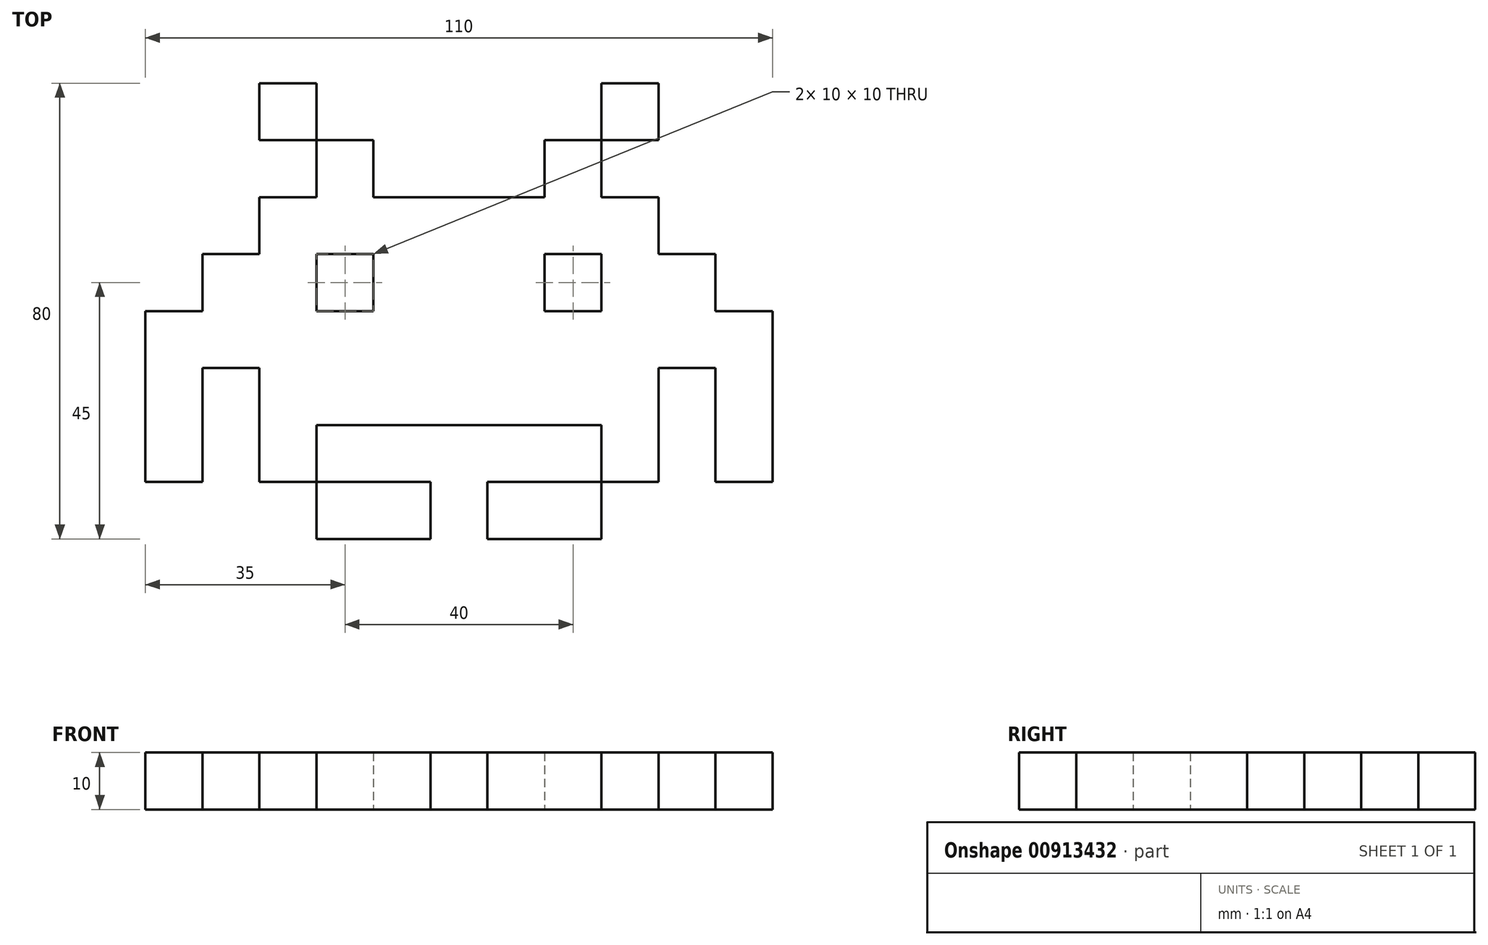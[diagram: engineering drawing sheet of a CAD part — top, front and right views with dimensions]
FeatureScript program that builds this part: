
annotation { "Feature Type Name" : "Feature", "Feature Type Description" : "" }
export const myFeature = defineFeature(function(context is Context, id is Id, definition is map)
    precondition{}
    {
        {
            var Q0;
            Q0=qCreatedBy(makeId("Top.planeOp"),FACE);
            var sketch = newSketch(context, id + "F0", { "sketchPlane" : qUnion([Q0])});
            skLineSegment(sketch, "E0", {"start": v(-15, 5) * mm, "end": v(-15, -5) * mm});
            skLineSegment(sketch, "E1", {"start": v(-15, -5) * mm, "end": v(-25, -5) * mm});
            skLineSegment(sketch, "E2", {"start": v(-25, -5) * mm, "end": v(-25, 5) * mm});
            skLineSegment(sketch, "E3", {"start": v(-25, 5) * mm, "end": v(-15, 5) * mm});
            skLineSegment(sketch, "E4", {"start": v(15, 5) * mm, "end": v(15, -5) * mm});
            skLineSegment(sketch, "E5", {"start": v(15, -5) * mm, "end": v(25, -5) * mm});
            skLineSegment(sketch, "E6", {"start": v(25, -5) * mm, "end": v(25, 5) * mm});
            skLineSegment(sketch, "E7", {"start": v(25, 5) * mm, "end": v(15, 5) * mm});
            skPoint(sketch, "E8", {"position": v(-15, 0) * mm});
            skPoint(sketch, "E9", {"position": v(15, 0) * mm});
            skLineSegment(sketch, "E10", {"start": v(-15, 15) * mm, "end": v(15, 15) * mm});
            skLineSegment(sketch, "E11", {"start": v(15, 15) * mm, "end": v(15, 25) * mm});
            skLineSegment(sketch, "E12", {"start": v(15, 25) * mm, "end": v(25, 25) * mm});
            skLineSegment(sketch, "E13", {"start": v(25, 25) * mm, "end": v(25, 15) * mm});
            skLineSegment(sketch, "E14", {"start": v(25, 15) * mm, "end": v(35, 15) * mm});
            skLineSegment(sketch, "E15", {"start": v(35, 15) * mm, "end": v(35, 5) * mm});
            skLineSegment(sketch, "E16", {"start": v(35, 5) * mm, "end": v(45, 5) * mm});
            skLineSegment(sketch, "E17", {"start": v(45, 5) * mm, "end": v(45, -5) * mm});
            skLineSegment(sketch, "E18", {"start": v(45, -5) * mm, "end": v(55, -5) * mm});
            skLineSegment(sketch, "E19", {"start": v(55, -5) * mm, "end": v(55, -35) * mm});
            skPoint(sketch, "E20", {"position": v(0, 15) * mm});
            skLineSegment(sketch, "E21", {"start": v(55, -35) * mm, "end": v(45, -35) * mm});
            skLineSegment(sketch, "E22", {"start": v(45, -35) * mm, "end": v(45, -15) * mm});
            skLineSegment(sketch, "E23", {"start": v(45, -15) * mm, "end": v(35, -15) * mm});
            skLineSegment(sketch, "E24", {"start": v(35, -15) * mm, "end": v(35, -35) * mm});
            skLineSegment(sketch, "E25", {"start": v(35, -35) * mm, "end": v(25, -35) * mm});
            skLineSegment(sketch, "E26", {"start": v(25, -35) * mm, "end": v(25, -25) * mm});
            skLineSegment(sketch, "E27", {"start": v(25, -25) * mm, "end": v(-25, -25) * mm});
            skLineSegment(sketch, "E28", {"start": v(-25, -25) * mm, "end": v(-25, -35) * mm});
            skLineSegment(sketch, "E29", {"start": v(-25, -35) * mm, "end": v(-35, -35) * mm});
            skLineSegment(sketch, "E30", {"start": v(-35, -35) * mm, "end": v(-35, -15) * mm});
            skLineSegment(sketch, "E31", {"start": v(-35, -15) * mm, "end": v(-45, -15) * mm});
            skLineSegment(sketch, "E32", {"start": v(-45, -15) * mm, "end": v(-45, -35) * mm});
            skLineSegment(sketch, "E33", {"start": v(-45, -35) * mm, "end": v(-55, -35) * mm});
            skLineSegment(sketch, "E34", {"start": v(-55, -35) * mm, "end": v(-55, -5) * mm});
            skLineSegment(sketch, "E35", {"start": v(-55, -5) * mm, "end": v(-45, -5) * mm});
            skLineSegment(sketch, "E36", {"start": v(-45, -5) * mm, "end": v(-45, 5) * mm});
            skLineSegment(sketch, "E37", {"start": v(-45, 5) * mm, "end": v(-35, 5) * mm});
            skLineSegment(sketch, "E38", {"start": v(-35, 5) * mm, "end": v(-35, 15) * mm});
            skLineSegment(sketch, "E39", {"start": v(-35, 15) * mm, "end": v(-25, 15) * mm});
            skLineSegment(sketch, "E40", {"start": v(-25, 15) * mm, "end": v(-25, 25) * mm});
            skLineSegment(sketch, "E41", {"start": v(-25, 25) * mm, "end": v(-15, 25) * mm});
            skLineSegment(sketch, "E42", {"start": v(-15, 25) * mm, "end": v(-15, 15) * mm});
            skLineSegment(sketch, "E43", {"start": v(-25, 25) * mm, "end": v(-25, 35) * mm});
            skLineSegment(sketch, "E44", {"start": v(-25, 35) * mm, "end": v(-35, 35) * mm});
            skLineSegment(sketch, "E45", {"start": v(-35, 35) * mm, "end": v(-35, 25) * mm});
            skLineSegment(sketch, "E46", {"start": v(-35, 25) * mm, "end": v(-25, 25) * mm});
            skLineSegment(sketch, "E47", {"start": v(25, 25) * mm, "end": v(25, 35) * mm});
            skLineSegment(sketch, "E48", {"start": v(25, 35) * mm, "end": v(35, 35) * mm});
            skLineSegment(sketch, "E49", {"start": v(35, 35) * mm, "end": v(35, 25) * mm});
            skLineSegment(sketch, "E50", {"start": v(35, 25) * mm, "end": v(25, 25) * mm});
            skLineSegment(sketch, "E51", {"start": v(-25, -35) * mm, "end": v(-25, -45) * mm});
            skLineSegment(sketch, "E52", {"start": v(-25, -45) * mm, "end": v(-5, -45) * mm});
            skLineSegment(sketch, "E53", {"start": v(-5, -45) * mm, "end": v(-5, -35) * mm});
            skLineSegment(sketch, "E54", {"start": v(-5, -35) * mm, "end": v(-25, -35) * mm});
            skLineSegment(sketch, "E55", {"start": v(25, -35) * mm, "end": v(25, -45) * mm});
            skLineSegment(sketch, "E56", {"start": v(25, -45) * mm, "end": v(5, -45) * mm});
            skLineSegment(sketch, "E57", {"start": v(5, -45) * mm, "end": v(5, -35) * mm});
            skLineSegment(sketch, "E58", {"start": v(5, -35) * mm, "end": v(25, -35) * mm});
            skSolve(sketch);
        }
        {
            var Q0;
            Q0=makeQuery(id+"F0.imprint","IMPRINT",FACE,{"disambiguationData":[TD([[makeQuery(id+"F0.imprint","IMPRINT",EDGE,{"derivedFrom":sQuery(id+"F0.wireOp",EDGE,"E0")}),1.0]])]});
            var Q1;
            Q1=makeQuery(id+"F0.imprint","IMPRINT",FACE,{"disambiguationData":[TD([[makeQuery(id+"F0.imprint","IMPRINT",EDGE,{"derivedFrom":sQuery(id+"F0.wireOp",EDGE,"E43")}),1.0]])]});
            var Q2;
            Q2=makeQuery(id+"F0.imprint","IMPRINT",FACE,{"disambiguationData":[TD([[makeQuery(id+"F0.imprint","IMPRINT",EDGE,{"derivedFrom":sQuery(id+"F0.wireOp",EDGE,"E51")}),1.0]])]});
            var Q3;
            Q3=makeQuery(id+"F0.imprint","IMPRINT",FACE,{"disambiguationData":[TD([[makeQuery(id+"F0.imprint","IMPRINT",EDGE,{"derivedFrom":sQuery(id+"F0.wireOp",EDGE,"E47")}),-1.0]])]});
            var Q4;
            Q4=makeQuery(id+"F0.imprint","IMPRINT",FACE,{"disambiguationData":[TD([[makeQuery(id+"F0.imprint","IMPRINT",EDGE,{"derivedFrom":sQuery(id+"F0.wireOp",EDGE,"E55")}),-1.0]])]});
            extrude(context, id + "F1", {"entities" : qUnion([Q0, Q1, Q2, Q3, Q4]), "depth" : 10 * mm, "offsetDistance" : 25 * mm});
        }
    });
